# Revit family: VLGFP2001-7DAWSxxxxxxxx
name_source: partatom
category: Leuchten
units: mm (PartAtom-declared; Revit-internal decimal feet)

## family parameters
Basisbauteil = Fläche
Beim Laden mit Abzugskörper schneiden = Nein
Bemaßung runder Anschluss = Durchmesser verwenden
Gemeinsam genutzt = Nein
Lichtquelle = Ja
OmniClass-Nummer = 23.80.70.11
OmniClass-Titel = Luminaries for Internal Lighting
Raumberechnungspunkt = Nein
Teiletyp = Normal

## types (10) — shared parameters
Baugruppenkennzeichen = D5020200
Emissionsform beim Rendern sichtbar = Nein
Farbfilter = 16777215
Farbtemperaturverschiebung bei Dämpfen der Lampe = <Keine Auswahl>
Hersteller = RIDI Leuchten GmbH
Lampe = LED
Neigungswinkel = 90.00°
URL = www.ridi.de
Von Breite des Rechtecks ausssenden = 1969 mm
Von Länge des Rechtecks aussenden = 27 mm  [stored 0.0885827 ft]
brand = RIDI
conformity mark = CE
electrical safety class = 1
height = 66 mm  [stored 0.216535 ft]
ingress protection (IP) code = IP54
length = 2000 mm  [stored 6.56168 ft]
nominal frequency = 50-60Hz
nominal voltage = 230
voltage type (AC, DC, UC) = AC
weight = 2,421
width = 67 mm
zero-valued in all types: Vorgabe-Ansicht

## per-type parameters (varying)
| type | Datei für fotometrisches Netz | Modell | Scheinlast | rated input power |
| VLGFP2001-7DAWS830E1000 | VLGFP1501-5NDWS840E0750.IES | 1561379 | 73 VA | 73 |
| VLGFP2001-7DAWS840B1100 | VLGFP1501-5NDWS840B0800.IES | 1561380 | 73 VA | 73 |
| VLGFP2001-7DAWS840E1100 | VLGFP1501-5NDWS840E0750.IES | 1561381 | 73 VA | 73 |
| VLGFP2001-7DAWS865B1100 | VLGFP1501-5NDWS840B0800.IES | 1561382 | 73 VA | 73 |
| VLGFP2001-7DAWS865E1100 | VLGFP1501-5NDWS840E0750.IES | 1561383 | 73 VA | 73 |
| VLGFP2001-7DAWS830B1100 | VLGFP1501-5NDWS840B0800.IES | 1561378 | 73 VA | 73 |
| VLGFP2001-7DAWS840B2100 | VLGFP1501-5NDWS840B0800.IES | 1561403 | 133 VA | 133 |
| VLGFP2001-7DAWS850B2100 | VLGFP1501-5NDWS840B0800.IES | 1561406 | 133 VA | 133 |
| VLGFP2001-7DAWS840E2000 | VLGFP1501-5NDWS840E0750.IES | 1561404 | 133 VA | 133 |
| VLGFP2001-7DAWS850E2000 | VLGFP1501-5NDWS840E0750.IES | 1561405 | 133 VA | 133 |

note: column(s) folded — value = type name in every type: product name

note: [stored X ft] marks values corroborated as IEEE doubles in the binary element streams (Revit-internal decimal feet)
